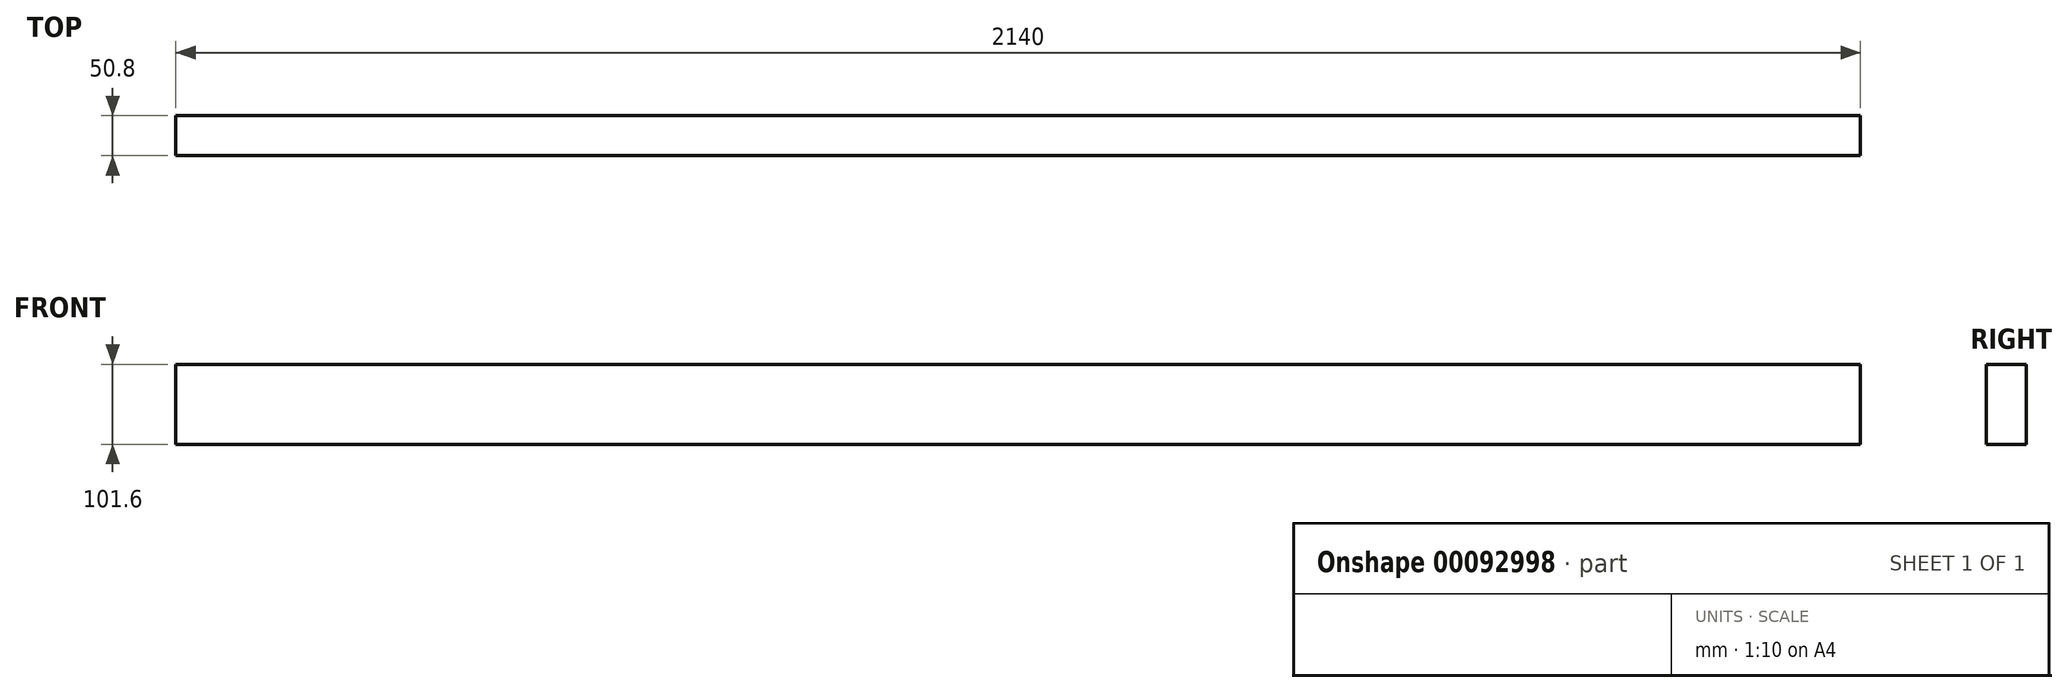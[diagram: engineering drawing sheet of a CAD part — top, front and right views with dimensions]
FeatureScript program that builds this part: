
annotation { "Feature Type Name" : "Feature", "Feature Type Description" : "" }
export const myFeature = defineFeature(function(context is Context, id is Id, definition is map)
    precondition{}
    {
        {
            var Q0;
            Q0=qCreatedBy(makeId("Top.planeOp"),FACE);
            var sketch = newSketch(context, id + "F0", { "sketchPlane" : qUnion([Q0])});
            skLineSegment(sketch, "E0.bottom", {"start": v(-1070, 25.4) * mm, "end": v(1070, 25.4) * mm});
            skLineSegment(sketch, "E0.top", {"start": v(-1070, -25.4) * mm, "end": v(1070, -25.4) * mm});
            skLineSegment(sketch, "E1", {"start": v(-1070, -25.4) * mm, "end": v(-1070, 25.4) * mm});
            skLineSegment(sketch, "E2", {"start": v(1070, -25.4) * mm, "end": v(1070, 25.4) * mm});
            skSolve(sketch);
        }
        {
            var Q0;
            Q0 = qSketchRegion(id + "F0", true);
            extrude(context, id + "F1", {"entities" : qUnion([Q0]), "oppositeDirection" : true, "depth" : 101.6 * mm});
        }
    });
